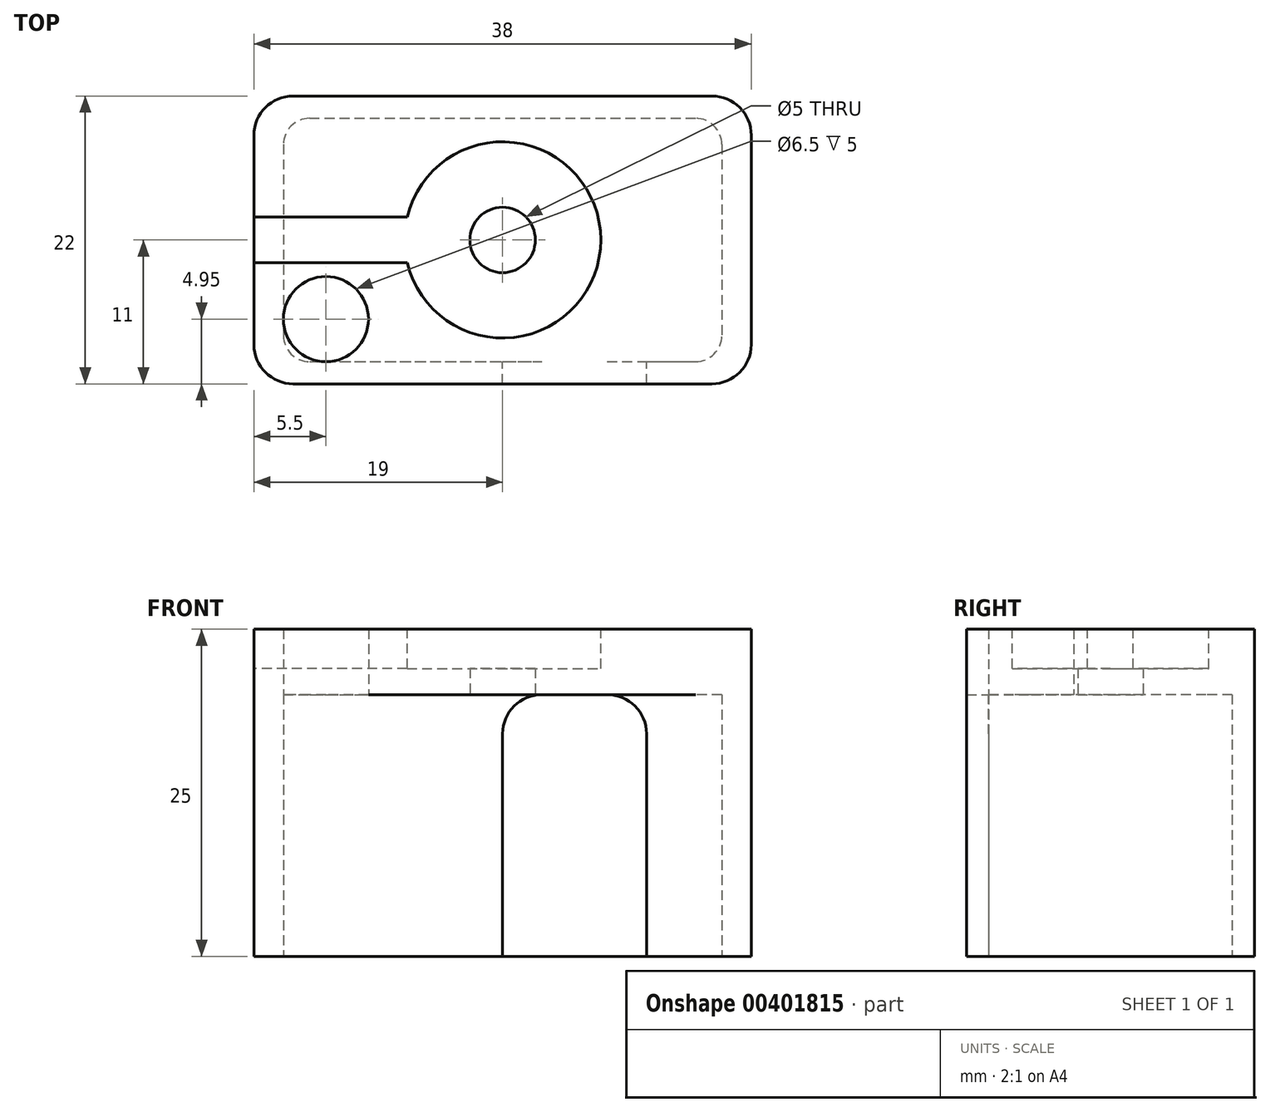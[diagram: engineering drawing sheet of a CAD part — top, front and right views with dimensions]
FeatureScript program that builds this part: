
annotation { "Feature Type Name" : "Feature", "Feature Type Description" : "" }
export const myFeature = defineFeature(function(context is Context, id is Id, definition is map)
    precondition{}
    {
        {
            var Q0;
            Q0=qCreatedBy(makeId("Top.planeOp"),FACE);
            var sketch = newSketch(context, id + "F0", { "sketchPlane" : qUnion([Q0])});
            skLineSegment(sketch, "E0.bottom", {"start": v(-14.75, 9.3) * mm, "end": v(14.75, 9.3) * mm});
            skLineSegment(sketch, "E0.top", {"start": v(-14.75, -9.3) * mm, "end": v(14.75, -9.3) * mm});
            skLineSegment(sketch, "E0.left", {"start": v(-16.75, 7.3) * mm, "end": v(-16.75, -7.3) * mm});
            skLineSegment(sketch, "E0.right", {"start": v(16.75, 7.3) * mm, "end": v(16.75, -7.3) * mm});
            skPoint(sketch, "E1", {"position": v(0, 9.3) * mm});
            skPoint(sketch, "E2", {"position": v(-16.75, 0) * mm});
            skPoint(sketch, "E3.visualSharp", {"position": v(-16.75, 9.3) * mm});
            skArc(sketch, "E3.filletArc", {"start": v(-14.75, 9.3) * mm, "mid": v(-16.16, 8.71) * mm, "end": v(-16.75, 7.3) * mm});
            skPoint(sketch, "E4.visualSharp", {"position": v(-16.75, -9.3) * mm});
            skArc(sketch, "E4.filletArc", {"start": v(-16.75, -7.3) * mm, "mid": v(-16.16, -8.71) * mm, "end": v(-14.75, -9.3) * mm});
            skPoint(sketch, "E5.visualSharp", {"position": v(16.75, -9.3) * mm});
            skArc(sketch, "E5.filletArc", {"start": v(14.75, -9.3) * mm, "mid": v(16.16, -8.71) * mm, "end": v(16.75, -7.3) * mm});
            skPoint(sketch, "E6.visualSharp", {"position": v(16.75, 9.3) * mm});
            skArc(sketch, "E6.filletArc", {"start": v(16.75, 7.3) * mm, "mid": v(16.16, 8.71) * mm, "end": v(14.75, 9.3) * mm});
            skLineSegment(sketch, "E7.bottom", {"start": v(-19, 11) * mm, "end": v(19, 11) * mm});
            skLineSegment(sketch, "E7.top", {"start": v(-19, -11) * mm, "end": v(19, -11) * mm});
            skLineSegment(sketch, "E7.left", {"start": v(-19, 11) * mm, "end": v(-19, -11) * mm});
            skLineSegment(sketch, "E7.right", {"start": v(19, 11) * mm, "end": v(19, -11) * mm});
            skPoint(sketch, "E8", {"position": v(0, 11) * mm});
            skPoint(sketch, "E9", {"position": v(-19, 0) * mm});
            skSolve(sketch);
        }
        {
            var Q0;
            Q0=makeQuery(id+"F0.imprint","IMPRINT",FACE,{"disambiguationData":[TD([[makeQuery(id+"F0.imprint","IMPRINT",EDGE,{"derivedFrom":sQuery(id+"F0.wireOp",EDGE,"E0.bottom")}),1.0]])]});
            extrude(context, id + "F1", {"entities" : qUnion([Q0]), "depth" : 20 * mm});
        }
        {
            var Q0;
            Q0=makeQuery(id+"F1.opExtrude","CAP_FACE",FACE,{"disambiguationData":[OSD([sQuery(id+"F0.wireOp",EDGE,"E0.bottom"),sQuery(id+"F0.wireOp",EDGE,"E0.top"),sQuery(id+"F0.wireOp",EDGE,"E0.left"),sQuery(id+"F0.wireOp",EDGE,"E0.right"),sQuery(id+"F0.wireOp",EDGE,"E3.filletArc"),sQuery(id+"F0.wireOp",EDGE,"E4.filletArc"),sQuery(id+"F0.wireOp",EDGE,"E5.filletArc"),sQuery(id+"F0.wireOp",EDGE,"E6.filletArc"),sQuery(id+"F0.wireOp",EDGE,"E7.bottom"),sQuery(id+"F0.wireOp",EDGE,"E7.top"),sQuery(id+"F0.wireOp",EDGE,"E7.left"),sQuery(id+"F0.wireOp",EDGE,"E7.right")])],"isStart":false});
            var sketch = newSketch(context, id + "F2", { "sketchPlane" : qUnion([Q0])});
            skLineSegment(sketch, "E10.bottom", {"start": v(-19, 11) * mm, "end": v(19, 11) * mm});
            skLineSegment(sketch, "E10.top", {"start": v(-19, -11) * mm, "end": v(19, -11) * mm});
            skLineSegment(sketch, "E10.left", {"start": v(-19, 11) * mm, "end": v(-19, -11) * mm});
            skLineSegment(sketch, "E10.right", {"start": v(19, 11) * mm, "end": v(19, -11) * mm});
            skSolve(sketch);
        }
        {
            var Q0;
            Q0 = qSketchRegion(id + "F2", true);
            extrude(context, id + "F3", {"entities" : qUnion([Q0]), "operationType" : NewBodyOperationType.ADD, "depth" : 5 * mm});
        }
        {
            var Q0;
            Q0=makeQuery(id+"F3.opExtrude","CAP_FACE",FACE,{"disambiguationData":[OSD([sQuery(id+"F2.wireOp",EDGE,"E10.bottom"),sQuery(id+"F2.wireOp",EDGE,"E10.top"),sQuery(id+"F2.wireOp",EDGE,"E10.left"),sQuery(id+"F2.wireOp",EDGE,"E10.right")])],"isStart":true});
            var sketch = newSketch(context, id + "F4", { "sketchPlane" : qUnion([Q0])});
            skCircle(sketch, "E11", {"center": v(-13.5, 6.05) * mm, "radius": 3.25 * mm});
            skPoint(sketch, "E12", {"position": v(-16.75, 6.05) * mm});
            skPoint(sketch, "E13", {"position": v(-13.5, 9.3) * mm});
            skCircle(sketch, "E14", {"center": v(0, 0) * mm, "radius": 2.5 * mm});
            skSolve(sketch);
        }
        {
            var Q0;
            {var subQ0=sQuery(id+"F4.wireOp",EDGE,"E11");var subQ1=makeQuery(id+"F4.imprint","INTERSECT",VERTEX,{"derivedFrom":[makeQuery(id+"F1.opExtrude","CAP_EDGE",EDGE,{"disambiguationData":[OSD([sQuery(id+"F0.wireOp",EDGE,"E0.top")])],"isStart":false}),subQ0]});Q0=makeQuery(id+"F4.imprint","IMPRINT",FACE,{"disambiguationData":[TD([[makeQuery(id+"F4.imprint","IMPRINT",EDGE,{"disambiguationData":[TD([[subQ1,-1.0]])],"derivedFrom":subQ0}),1.0]])]});}
            var Q1;
            Q1=makeQuery(id+"F4.imprint","IMPRINT",FACE,{"disambiguationData":[TD([[makeQuery(id+"F4.imprint","IMPRINT",EDGE,{"derivedFrom":sQuery(id+"F4.wireOp",EDGE,"E14")}),1.0]])]});
            extrude(context, id + "F5", {"entities" : qUnion([Q0, Q1]), "operationType" : NewBodyOperationType.REMOVE, "endBound" : BoundingType.UP_TO_NEXT, "oppositeDirection" : true, "depth" : 25 * mm});
        }
        {
            var Q0;
            Q0=makeQuery(id+"F3.opExtrude","CAP_FACE",FACE,{"disambiguationData":[OSD([sQuery(id+"F2.wireOp",EDGE,"E10.bottom"),sQuery(id+"F2.wireOp",EDGE,"E10.top"),sQuery(id+"F2.wireOp",EDGE,"E10.left"),sQuery(id+"F2.wireOp",EDGE,"E10.right")])],"isStart":false});
            var sketch = newSketch(context, id + "F6", { "sketchPlane" : qUnion([Q0])});
            skCircle(sketch, "E15", {"center": v(0, 0) * mm, "radius": 10 * mm});
            skCircle(sketch, "E16", {"center": v(0, 0) * mm, "radius": 7.5 * mm});
            skSolve(sketch);
        }
        {
            var Q0;
            Q0=makeQuery(id+"F6.imprint","IMPRINT",FACE,{"disambiguationData":[TD([[makeQuery(id+"F6.imprint","IMPRINT",EDGE,{"derivedFrom":sQuery(id+"F6.wireOp",EDGE,"E16")}),1.0]])]});
            extrude(context, id + "F7", {"entities" : qUnion([Q0]), "operationType" : NewBodyOperationType.REMOVE, "oppositeDirection" : true, "depth" : 3 * mm});
        }
        {
            var Q0;
            Q0=makeQuery(id+"F1.opExtrude","SWEPT_FACE",FACE,{"disambiguationData":[OSD([sQuery(id+"F0.wireOp",EDGE,"E0.top")])]});
            var sketch = newSketch(context, id + "F8", { "sketchPlane" : qUnion([Q0])});
            skLineSegment(sketch, "E17.bottom", {"start": v(-11, 20) * mm, "end": v(0, 20) * mm});
            skLineSegment(sketch, "E17.top", {"start": v(-11, 0) * mm, "end": v(0, 0) * mm});
            skLineSegment(sketch, "E17.left", {"start": v(-11, 20) * mm, "end": v(-11, 0) * mm});
            skLineSegment(sketch, "E17.right", {"start": v(0, 20) * mm, "end": v(0, 0) * mm});
            skSolve(sketch);
        }
        {
            var Q0;
            Q0=makeQuery(id+"F8.imprint","IMPRINT",FACE,{"disambiguationData":[TD([[makeQuery(id+"F8.imprint","IMPRINT",EDGE,{"derivedFrom":sQuery(id+"F8.wireOp",EDGE,"E17.bottom")}),1.0]])]});
            extrude(context, id + "F9", {"entities" : qUnion([Q0]), "operationType" : NewBodyOperationType.REMOVE, "endBound" : BoundingType.UP_TO_NEXT, "oppositeDirection" : true, "depth" : 25 * mm});
        }
        {
            var Q0;
            Q0=makeQuery(id+"F3.opExtrude","CAP_FACE",FACE,{"disambiguationData":[OSD([sQuery(id+"F2.wireOp",EDGE,"E10.bottom"),sQuery(id+"F2.wireOp",EDGE,"E10.top"),sQuery(id+"F2.wireOp",EDGE,"E10.left"),sQuery(id+"F2.wireOp",EDGE,"E10.right")])],"isStart":false});
            var sketch = newSketch(context, id + "F10", { "sketchPlane" : qUnion([Q0])});
            skLineSegment(sketch, "E18.bottom", {"start": v(-19, 1.75) * mm, "end": v(0, 1.75) * mm});
            skLineSegment(sketch, "E18.top", {"start": v(-19, -1.75) * mm, "end": v(0, -1.75) * mm});
            skLineSegment(sketch, "E18.left", {"start": v(-19, 1.75) * mm, "end": v(-19, -1.75) * mm});
            skLineSegment(sketch, "E18.right", {"start": v(0, 1.75) * mm, "end": v(0, -1.75) * mm});
            skPoint(sketch, "E19", {"position": v(-19, 0) * mm});
            skSolve(sketch);
        }
        {
            var Q0;
            {var subQ0=sQuery(id+"F10.wireOp",EDGE,"E18.left");Q0=makeQuery(id+"F10.imprint","IMPRINT",FACE,{"disambiguationData":[TD([[makeQuery(id+"F10.imprint","IMPRINT",EDGE,{"derivedFrom":subQ0}),1.0]])]});}
            var Q1;
            Q1=makeQuery(id+"F7.boolean.opBoolean","COPY",FACE,{"derivedFrom":makeQuery(id+"F7.opExtrude","CAP_FACE",FACE,{"disambiguationData":[OSD([sQuery(id+"F2.wireOp",EDGE,"E10.bottom"),sQuery(id+"F2.wireOp",EDGE,"E10.top"),sQuery(id+"F2.wireOp",EDGE,"E10.left"),sQuery(id+"F2.wireOp",EDGE,"E10.right"),sQuery(id+"F4.wireOp",EDGE,"E14"),sQuery(id+"F6.wireOp",EDGE,"E15")])],"isStart":false})});
            extrude(context, id + "F11", {"entities" : qUnion([Q0]), "operationType" : NewBodyOperationType.REMOVE, "endBound" : BoundingType.UP_TO_SURFACE, "oppositeDirection" : true, "endBoundEntityFace" : qUnion([Q1]), "depth" : 25 * mm});
        }
        {
            var Q0;
            Q0=makeQuery(id+"F3.boolean.opBoolean","MERGE",EDGE,{"derivedFrom":[makeQuery(id+"F1.opExtrude","SWEPT_EDGE",EDGE,{"disambiguationData":[OSD([sQuery(id+"F0.wireOp",EDGE,"E7.top"),sQuery(id+"F0.wireOp",EDGE,"E7.left")])]}),makeQuery(id+"F3.opExtrude","SWEPT_EDGE",EDGE,{"disambiguationData":[OSD([sQuery(id+"F2.wireOp",EDGE,"E10.top"),sQuery(id+"F2.wireOp",EDGE,"E10.left")])]})]});
            var Q1;
            Q1=makeQuery(id+"F3.boolean.opBoolean","MERGE",EDGE,{"derivedFrom":[makeQuery(id+"F1.opExtrude","SWEPT_EDGE",EDGE,{"disambiguationData":[OSD([sQuery(id+"F0.wireOp",EDGE,"E7.top"),sQuery(id+"F0.wireOp",EDGE,"E7.right")])]}),makeQuery(id+"F3.opExtrude","SWEPT_EDGE",EDGE,{"disambiguationData":[OSD([sQuery(id+"F2.wireOp",EDGE,"E10.top"),sQuery(id+"F2.wireOp",EDGE,"E10.right")])]})]});
            var Q2;
            Q2=makeQuery(id+"F3.boolean.opBoolean","MERGE",EDGE,{"derivedFrom":[makeQuery(id+"F1.opExtrude","SWEPT_EDGE",EDGE,{"disambiguationData":[OSD([sQuery(id+"F0.wireOp",EDGE,"E7.bottom"),sQuery(id+"F0.wireOp",EDGE,"E7.right")])]}),makeQuery(id+"F3.opExtrude","SWEPT_EDGE",EDGE,{"disambiguationData":[OSD([sQuery(id+"F2.wireOp",EDGE,"E10.bottom"),sQuery(id+"F2.wireOp",EDGE,"E10.right")])]})]});
            var Q3;
            Q3=makeQuery(id+"F3.boolean.opBoolean","MERGE",EDGE,{"derivedFrom":[makeQuery(id+"F1.opExtrude","SWEPT_EDGE",EDGE,{"disambiguationData":[OSD([sQuery(id+"F0.wireOp",EDGE,"E7.bottom"),sQuery(id+"F0.wireOp",EDGE,"E7.left")])]}),makeQuery(id+"F3.opExtrude","SWEPT_EDGE",EDGE,{"disambiguationData":[OSD([sQuery(id+"F2.wireOp",EDGE,"E10.bottom"),sQuery(id+"F2.wireOp",EDGE,"E10.left")])]})]});
            fillet(context, id + "F12", {"entities" : qUnion([Q0, Q1, Q2, Q3]), "radius" : 3 * mm, "tangentPropagation" : true, "allowEdgeOverflow" : false});
        }
        {
            var Q0;
            Q0=makeQuery(id+"F9.boolean.opBoolean","COPY",EDGE,{"derivedFrom":makeQuery(id+"F9.opExtrude","SWEPT_EDGE",EDGE,{"disambiguationData":[OSD([sQuery(id+"F0.wireOp",EDGE,"E0.top"),sQuery(id+"F8.wireOp",EDGE,"E17.bottom"),sQuery(id+"F8.wireOp",EDGE,"E17.right")])]})});
            var Q1;
            Q1=makeQuery(id+"F9.boolean.opBoolean","COPY",EDGE,{"derivedFrom":makeQuery(id+"F9.opExtrude","SWEPT_EDGE",EDGE,{"disambiguationData":[OSD([sQuery(id+"F0.wireOp",EDGE,"E0.top"),sQuery(id+"F8.wireOp",EDGE,"E17.bottom"),sQuery(id+"F8.wireOp",EDGE,"E17.left")])]})});
            fillet(context, id + "F13", {"entities" : qUnion([Q0, Q1]), "radius" : 3 * mm, "tangentPropagation" : true, "allowEdgeOverflow" : false});
        }
    });
